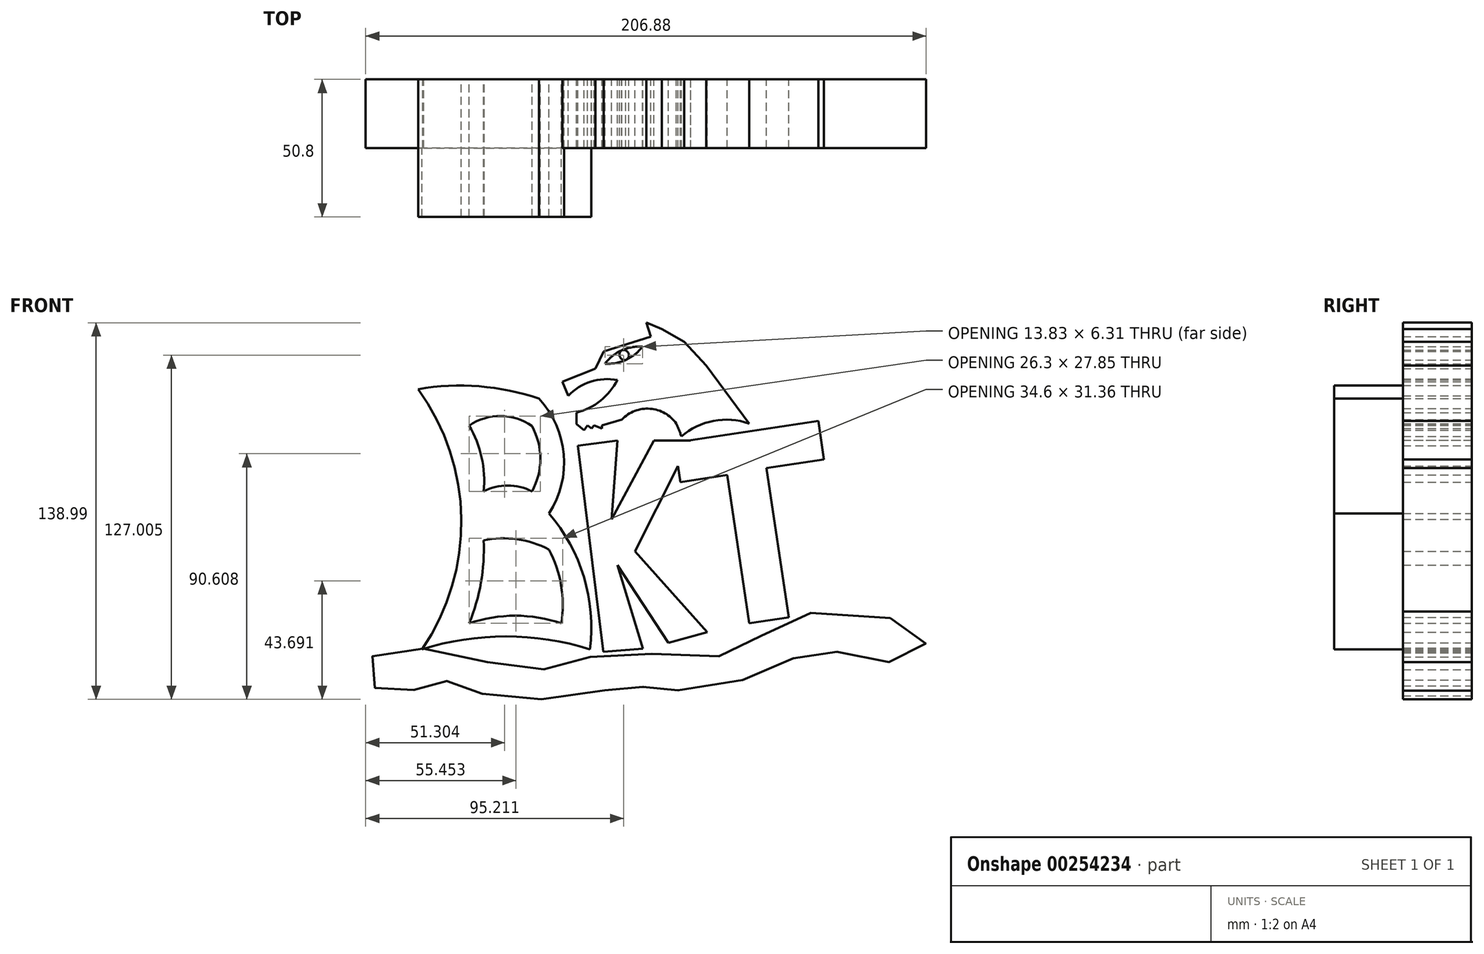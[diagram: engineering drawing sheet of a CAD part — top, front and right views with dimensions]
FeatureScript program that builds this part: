
annotation { "Feature Type Name" : "Feature", "Feature Type Description" : "" }
export const myFeature = defineFeature(function(context is Context, id is Id, definition is map)
    precondition{}
    {
        {
            var Q0;
            Q0=qCreatedBy(makeId("Front.planeOp"),FACE);
            var sketch = newSketch(context, id + "F0", { "sketchPlane" : qUnion([Q0])});
            skArc(sketch, "E0", {"start": v(-46.83, -52.73) * mm, "mid": v(-32.37, -4.47) * mm, "end": v(-48.3, 43.32) * mm});
            skArc(sketch, "E1", {"start": v(15.12, -52.73) * mm, "mid": v(-15.85, -47.97) * mm, "end": v(-46.83, -52.73) * mm});
            skArc(sketch, "E2", {"start": v(15.12, -52.73) * mm, "mid": v(12.88, -26.05) * mm, "end": v(0, -2.58) * mm});
            skArc(sketch, "E3", {"start": v(0, -2.58) * mm, "mid": v(5.43, 19.25) * mm, "end": v(-3.69, 39.82) * mm});
            skArc(sketch, "E4", {"start": v(-3.69, 39.82) * mm, "mid": v(-25.78, 44.35) * mm, "end": v(-48.3, 43.32) * mm});
            skArc(sketch, "E5", {"start": v(-24.15, 5.53) * mm, "mid": v(-24.86, 18.13) * mm, "end": v(-29.5, 29.87) * mm});
            skArc(sketch, "E6", {"start": v(-6.27, 5.53) * mm, "mid": v(-15.2, 7.74) * mm, "end": v(-24.15, 5.53) * mm});
            skArc(sketch, "E7", {"start": v(-6.27, 5.53) * mm, "mid": v(-3.2, 17.6) * mm, "end": v(-6.27, 29.68) * mm});
            skArc(sketch, "E8", {"start": v(-6.27, 29.68) * mm, "mid": v(-17.85, 33.39) * mm, "end": v(-29.5, 29.87) * mm});
            skArc(sketch, "E9", {"start": v(-29.5, -43.14) * mm, "mid": v(-25.1, -28.14) * mm, "end": v(-24.15, -12.54) * mm});
            skArc(sketch, "E10", {"start": v(4.6, -43.14) * mm, "mid": v(-12.44, -40.32) * mm, "end": v(-29.5, -43.14) * mm});
            skArc(sketch, "E11", {"start": v(4.6, -43.14) * mm, "mid": v(4.48, -29.13) * mm, "end": v(0, -15.85) * mm});
            skArc(sketch, "E12", {"start": v(0, -15.85) * mm, "mid": v(-11.79, -12.1) * mm, "end": v(-24.15, -12.54) * mm});
            skSolve(sketch);
        }
        {
            var Q0;
            Q0=makeQuery(id+"F0.imprint","IMPRINT",FACE,{"disambiguationData":[TD([[makeQuery(id+"F0.imprint","IMPRINT",EDGE,{"derivedFrom":sQuery(id+"F0.wireOp",EDGE,"E0")}),-1.0]])]});
            extrude(context, id + "F1", {"entities" : qUnion([Q0]), "depth" : 25.4 * mm});
        }
        {
            var Q0;
            Q0=qCreatedBy(makeId("Front.planeOp"),FACE);
            var sketch = newSketch(context, id + "F2", { "sketchPlane" : qUnion([Q0])});
            skLineSegment(sketch, "E13", {"start": v(20.1, -53.65) * mm, "end": v(10.7, 22.5) * mm});
            skLineSegment(sketch, "E14", {"start": v(10.7, 22.5) * mm, "end": v(25.22, 24.28) * mm});
            skLineSegment(sketch, "E15", {"start": v(25.22, 24.28) * mm, "end": v(23.04, -4.8) * mm});
            skLineSegment(sketch, "E16", {"start": v(23.04, -4.8) * mm, "end": v(38.71, 24.28) * mm});
            skLineSegment(sketch, "E17", {"start": v(38.71, 24.28) * mm, "end": v(52.36, 24.28) * mm});
            skLineSegment(sketch, "E18", {"start": v(52.36, 24.28) * mm, "end": v(31.7, -16.6) * mm});
            skLineSegment(sketch, "E19", {"start": v(31.7, -16.6) * mm, "end": v(58.44, -46.46) * mm});
            skLineSegment(sketch, "E20", {"start": v(58.44, -46.46) * mm, "end": v(44.06, -50.33) * mm});
            skLineSegment(sketch, "E21", {"start": v(44.06, -50.33) * mm, "end": v(25.22, -21.57) * mm});
            skLineSegment(sketch, "E22", {"start": v(25.22, -21.57) * mm, "end": v(34.66, -52.54) * mm});
            skLineSegment(sketch, "E23", {"start": v(34.66, -52.54) * mm, "end": v(20.1, -53.65) * mm});
            skSolve(sketch);
        }
        {
            var Q0;
            Q0 = qSketchRegion(id + "F2", true);
            extrude(context, id + "F3", {"entities" : qUnion([Q0]), "depth" : 25.4 * mm});
        }
        {
            var Q0;
            Q0=qCreatedBy(makeId("Front.planeOp"),FACE);
            var sketch = newSketch(context, id + "F4", { "sketchPlane" : qUnion([Q0])});
            skLineSegment(sketch, "E24", {"start": v(52.36, 24.52) * mm, "end": v(99.37, 31.52) * mm});
            skLineSegment(sketch, "E25", {"start": v(99.37, 31.52) * mm, "end": v(101.47, 17.4) * mm});
            skLineSegment(sketch, "E26", {"start": v(101.47, 17.4) * mm, "end": v(80.22, 14.23) * mm});
            skLineSegment(sketch, "E27", {"start": v(80.22, 14.23) * mm, "end": v(88.44, -40.96) * mm});
            skLineSegment(sketch, "E28", {"start": v(88.44, -40.96) * mm, "end": v(73.95, -43.12) * mm});
            skLineSegment(sketch, "E29", {"start": v(73.95, -43.12) * mm, "end": v(65.8, 11.6) * mm});
            skLineSegment(sketch, "E30", {"start": v(65.8, 11.6) * mm, "end": v(48.53, 9.02) * mm});
            skLineSegment(sketch, "E31", {"start": v(48.53, 9.02) * mm, "end": v(47.51, 15.9) * mm});
            skLineSegment(sketch, "E32", {"start": v(47.51, 15.9) * mm, "end": v(52.36, 24.52) * mm});
            skSolve(sketch);
        }
        {
            var Q0;
            Q0 = qSketchRegion(id + "F4", true);
            extrude(context, id + "F5", {"entities" : qUnion([Q0]), "operationType" : NewBodyOperationType.ADD, "depth" : 25.4 * mm});
        }
        {
            var Q0;
            Q0=qCreatedBy(makeId("Front.planeOp"),FACE);
            var sketch = newSketch(context, id + "F6", { "sketchPlane" : qUnion([Q0])});
            skFitSpline(sketch, "E33", {"points": [v(-67.47, -58.44) * mm, v(-46.09, -52.54) * mm, v(-4.42, -60.28) * mm, v(22.5, -54.2) * mm, v(68.4, -54.2) * mm, v(90.33, -40.56) * mm, v(138.82, -47.75) * mm, v(129.42, -57.15) * mm, v(100.66, -53.1) * mm, v(76.5, -62.5) * mm, v(38.53, -67.66) * mm, v(32.63, -66.18) * mm, v(0, -70.98) * mm, v(-32.82, -66.55) * mm, v(-41.66, -64.16) * mm, v(-59.36, -69.69) * mm, v(-67.47, -58.44) * mm]});
            skSolve(sketch);
        }
        {
            var Q0;
            Q0 = qSketchRegion(id + "F6", true);
            var Q1;
            Q1=makeQuery(id+"F1.opExtrude","CAP_FACE",FACE,{"disambiguationData":[OSD([sQuery(id+"F0.wireOp",EDGE,"E0"),sQuery(id+"F0.wireOp",EDGE,"E1"),sQuery(id+"F0.wireOp",EDGE,"E2"),sQuery(id+"F0.wireOp",EDGE,"E3"),sQuery(id+"F0.wireOp",EDGE,"E4"),sQuery(id+"F0.wireOp",EDGE,"E5"),sQuery(id+"F0.wireOp",EDGE,"E6"),sQuery(id+"F0.wireOp",EDGE,"E7"),sQuery(id+"F0.wireOp",EDGE,"E8"),sQuery(id+"F0.wireOp",EDGE,"E9"),sQuery(id+"F0.wireOp",EDGE,"E10"),sQuery(id+"F0.wireOp",EDGE,"E11"),sQuery(id+"F0.wireOp",EDGE,"E12")])],"isStart":false});
            extrude(context, id + "F7", {"entities" : qUnion([Q0, Q1]), "operationType" : NewBodyOperationType.ADD, "depth" : 25.4 * mm});
        }
        {
            var Q0;
            Q0=qCreatedBy(makeId("Front.planeOp"),FACE);
            var sketch = newSketch(context, id + "F8", { "sketchPlane" : qUnion([Q0])});
            skArc(sketch, "E34", {"start": v(34.47, 59) * mm, "mid": v(26.77, 57.6) * mm, "end": v(20.65, 52.73) * mm});
            skArc(sketch, "E35", {"start": v(20.65, 52.73) * mm, "mid": v(28.36, 54.1) * mm, "end": v(34.47, 59) * mm});
            skArc(sketch, "E36", {"start": v(28.36, 54.1) * mm, "mid": v(29.32, 56.65) * mm, "end": v(26.77, 57.6) * mm});
            skPoint(sketch, "E36.midSnap0", {"position": v(28.36, 54.1) * mm});
            skPoint(sketch, "E36.midSnap1", {"position": v(26.77, 57.6) * mm});
            skArc(sketch, "E37", {"start": v(26.77, 57.6) * mm, "mid": v(26.2, 55.23) * mm, "end": v(28.36, 54.1) * mm});
            skLineSegment(sketch, "E38", {"start": v(17.15, 50.88) * mm, "end": v(4.98, 46.09) * mm});
            skLineSegment(sketch, "E39", {"start": v(4.98, 46.09) * mm, "end": v(7.05, 40.83) * mm});
            skArc(sketch, "E40", {"start": v(25.26, 46.64) * mm, "mid": v(15.4, 46.08) * mm, "end": v(7.05, 40.83) * mm});
            skArc(sketch, "E41", {"start": v(10.14, 34.66) * mm, "mid": v(18.98, 39.04) * mm, "end": v(25.26, 46.64) * mm});
            skLineSegment(sketch, "E42", {"start": v(10.14, 34.66) * mm, "end": v(10.14, 30.42) * mm});
            skLineSegment(sketch, "E43", {"start": v(10.14, 30.42) * mm, "end": v(12.9, 28.2) * mm});
            skLineSegment(sketch, "E44", {"start": v(12.9, 28.2) * mm, "end": v(14.27, 29.91) * mm});
            skLineSegment(sketch, "E45", {"start": v(14.27, 29.91) * mm, "end": v(15.71, 28.76) * mm});
            skLineSegment(sketch, "E46", {"start": v(15.71, 28.76) * mm, "end": v(16.63, 29.91) * mm});
            skLineSegment(sketch, "E47", {"start": v(16.63, 29.91) * mm, "end": v(19.54, 28.76) * mm});
            skLineSegment(sketch, "E48", {"start": v(19.54, 28.76) * mm, "end": v(19.54, 29.91) * mm});
            skLineSegment(sketch, "E49", {"start": v(19.54, 29.91) * mm, "end": v(26.92, 32.08) * mm});
            skArc(sketch, "E50", {"start": v(47.01, 30.6) * mm, "mid": v(37.31, 36.09) * mm, "end": v(26.92, 32.08) * mm});
            skArc(sketch, "E51", {"start": v(48.85, 25.8) * mm, "mid": v(48, 28.23) * mm, "end": v(47.01, 30.6) * mm});
            skArc(sketch, "E52", {"start": v(73.93, 30.6) * mm, "mid": v(60.74, 31.62) * mm, "end": v(48.85, 25.8) * mm});
            skLineSegment(sketch, "E53", {"start": v(73.93, 30.6) * mm, "end": v(58.07, 51.99) * mm});
            skLineSegment(sketch, "E54", {"start": v(58.07, 51.99) * mm, "end": v(49.94, 60.79) * mm});
            skLineSegment(sketch, "E55", {"start": v(49.94, 60.79) * mm, "end": v(41.66, 65.45) * mm});
            skLineSegment(sketch, "E56", {"start": v(41.66, 65.45) * mm, "end": v(35.95, 67.84) * mm});
            skLineSegment(sketch, "E57", {"start": v(35.95, 67.84) * mm, "end": v(37.57, 62.7) * mm});
            skLineSegment(sketch, "E58", {"start": v(37.57, 62.7) * mm, "end": v(20.16, 57.23) * mm});
            skLineSegment(sketch, "E59", {"start": v(20.16, 57.23) * mm, "end": v(17.15, 50.88) * mm});
            skSolve(sketch);
        }
        {
            var Q0;
            {var subQ4=sQuery(id+"F8.wireOp",EDGE,"E36");Q0=makeQuery(id+"F8.imprint","IMPRINT",FACE,{"disambiguationData":[TD([[makeQuery(id+"F8.imprint","IMPRINT",EDGE,{"derivedFrom":subQ4}),-1.0]])]});}
            var Q1;
            {var subQ3=sQuery(id+"F8.wireOp",EDGE,"E37");Q1=makeQuery(id+"F8.imprint","IMPRINT",FACE,{"disambiguationData":[TD([[makeQuery(id+"F8.imprint","IMPRINT",EDGE,{"derivedFrom":subQ3}),-1.0]])]});}
            extrude(context, id + "F9", {"entities" : qUnion([Q0, Q1]), "depth" : 25.4 * mm});
        }
        {
            var Q0;
            Q0 = qSketchRegion(id + "F8", true);
            extrude(context, id + "F10", {"entities" : qUnion([Q0]), "depth" : 25.4 * mm});
        }
    });
